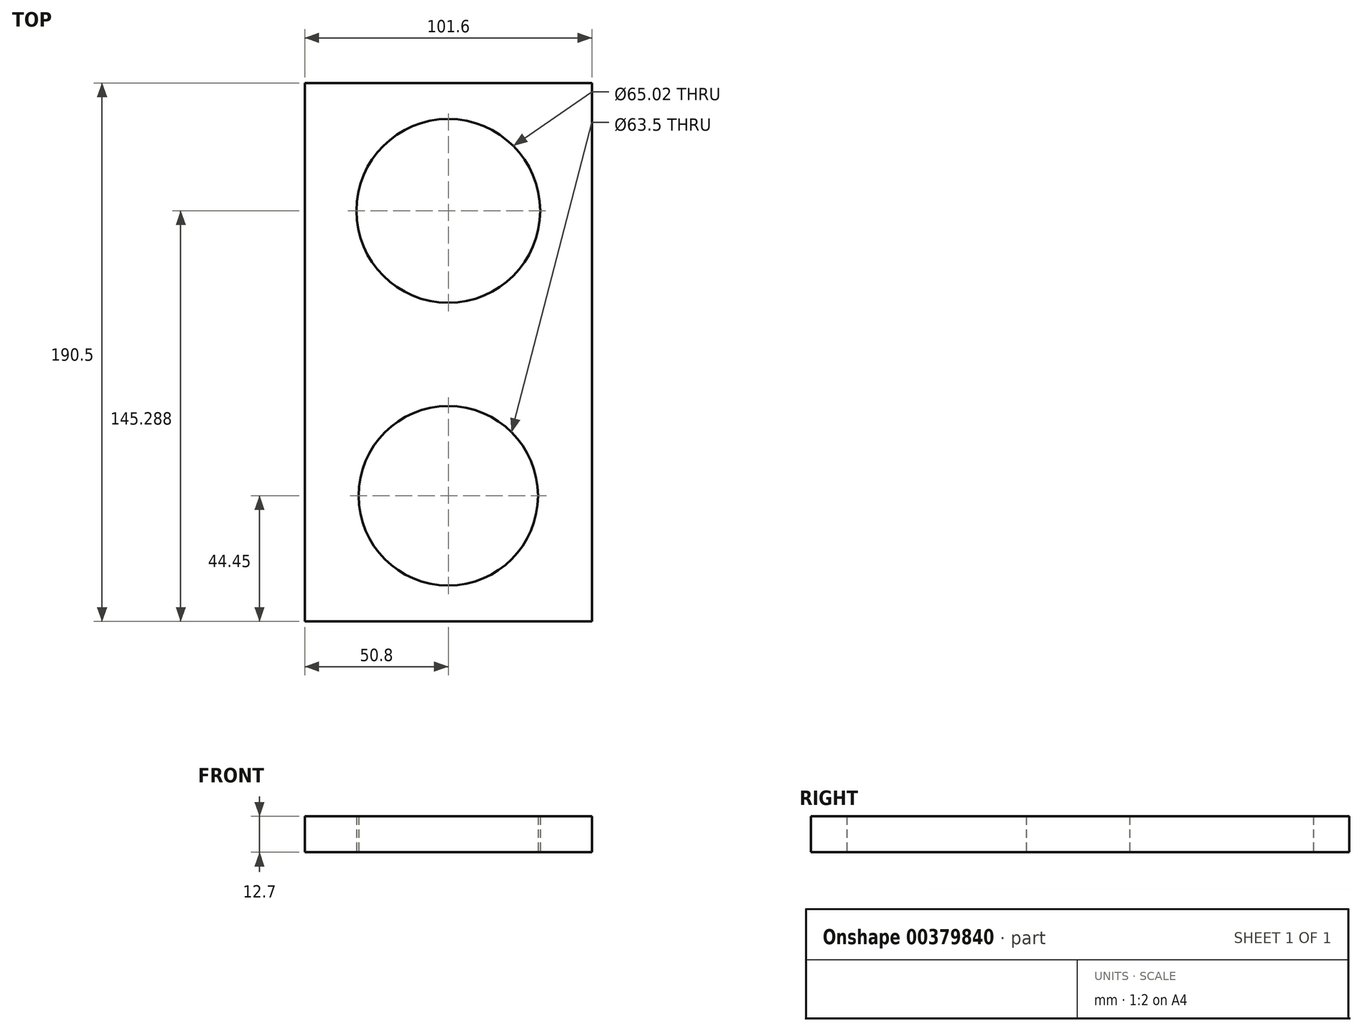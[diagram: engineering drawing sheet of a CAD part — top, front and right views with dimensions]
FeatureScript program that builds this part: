
annotation { "Feature Type Name" : "Feature", "Feature Type Description" : "" }
export const myFeature = defineFeature(function(context is Context, id is Id, definition is map)
    precondition{}
    {
        {
            var Q0;
            Q0=qCreatedBy(makeId("Top.planeOp"),FACE);
            var sketch = newSketch(context, id + "F0", { "sketchPlane" : qUnion([Q0])});
            skLineSegment(sketch, "E0.bottom", {"start": v(0, 0) * mm, "end": v(101.6, 0) * mm});
            skLineSegment(sketch, "E0.top", {"start": v(0, 190.5) * mm, "end": v(101.6, 190.5) * mm});
            skLineSegment(sketch, "E0.left", {"start": v(0, 0) * mm, "end": v(0, 190.5) * mm});
            skLineSegment(sketch, "E0.right", {"start": v(101.6, 0) * mm, "end": v(101.6, 190.5) * mm});
            skCircle(sketch, "E1", {"center": v(50.8, 145.29) * mm, "radius": 32.51 * mm});
            skPoint(sketch, "E1.centerSnap0", {"position": v(50.8, 190.5) * mm});
            skCircle(sketch, "E2", {"center": v(50.8, 44.45) * mm, "radius": 31.75 * mm});
            skPoint(sketch, "E2.centerSnap0", {"position": v(50.8, 0) * mm});
            skSolve(sketch);
        }
        {
            var Q0;
            Q0=qSketchRegion(id+"F0",true);
            extrude(context, id + "F1", {"entities" : qUnion([Q0]), "depth" : 12.7 * mm});
        }
    });
